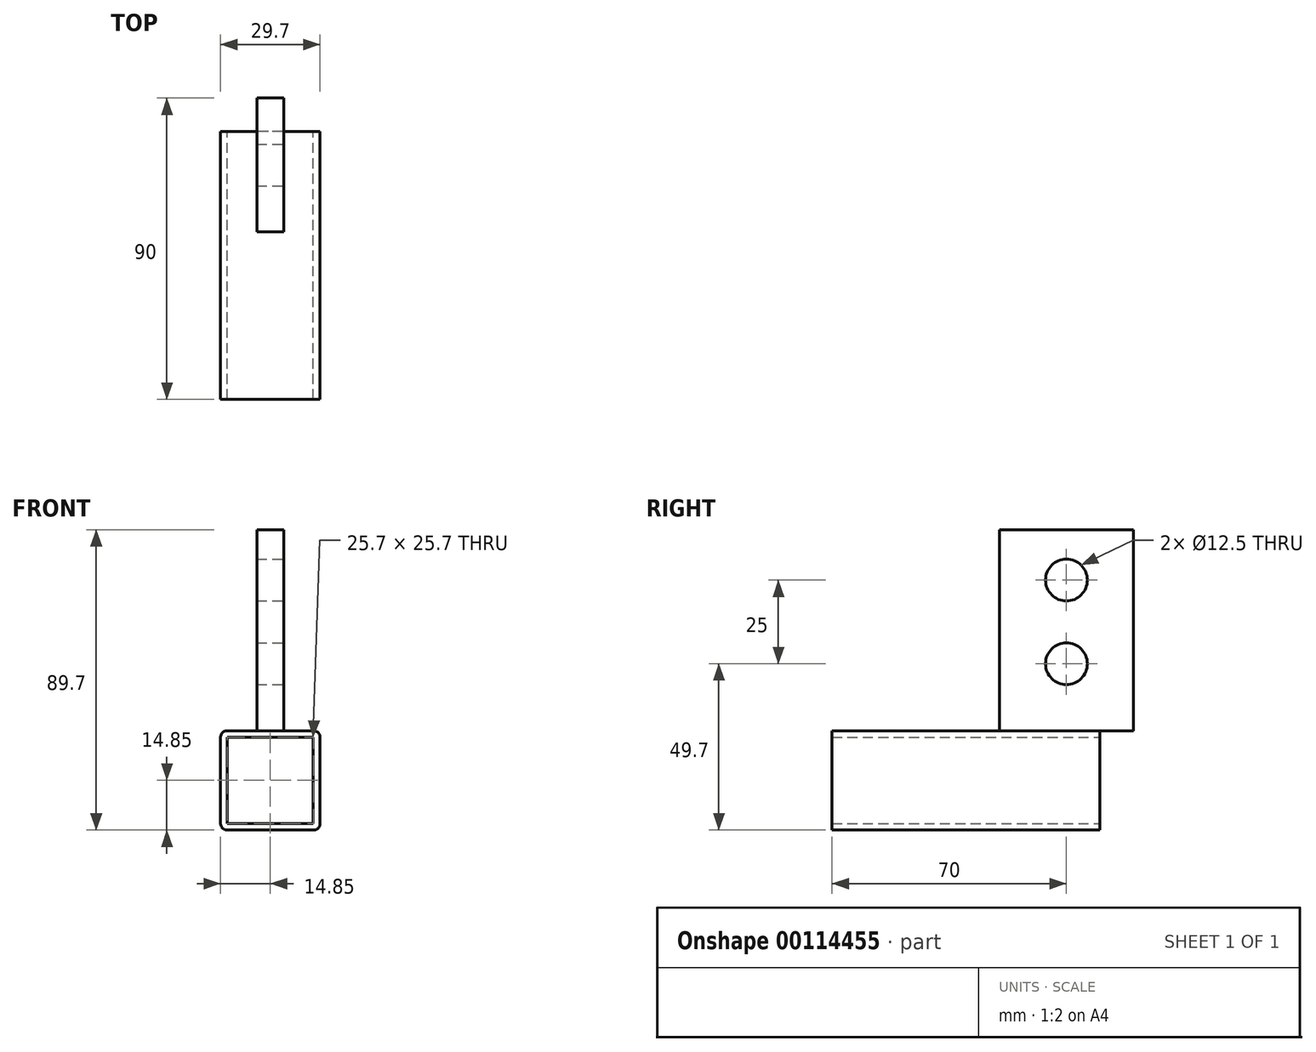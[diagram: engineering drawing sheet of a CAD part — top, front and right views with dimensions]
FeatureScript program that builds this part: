
annotation { "Feature Type Name" : "Feature", "Feature Type Description" : "" }
export const myFeature = defineFeature(function(context is Context, id is Id, definition is map)
    precondition{}
    {
        {
            var Q0;
            Q0=qCreatedBy(makeId("Front.planeOp"),FACE);
            var sketch = newSketch(context, id + "F0", { "sketchPlane" : qUnion([Q0])});
            skLineSegment(sketch, "E0.bottom", {"start": v(12.85, -14.85) * mm, "end": v(-12.85, -14.85) * mm});
            skLineSegment(sketch, "E0.top", {"start": v(12.85, 14.85) * mm, "end": v(-12.85, 14.85) * mm});
            skLineSegment(sketch, "E0.left", {"start": v(14.85, -12.85) * mm, "end": v(14.85, 12.85) * mm});
            skLineSegment(sketch, "E0.right", {"start": v(-14.85, -12.85) * mm, "end": v(-14.85, 12.85) * mm});
            skPoint(sketch, "E0.middle", {"position": v(0, 0) * mm});
            skLineSegment(sketch, "E1.0", {"start": v(-12.85, -12.85) * mm, "end": v(-12.85, 12.85) * mm});
            skLineSegment(sketch, "E1.1", {"start": v(12.85, -12.85) * mm, "end": v(-12.85, -12.85) * mm});
            skLineSegment(sketch, "E1.2", {"start": v(12.85, -12.85) * mm, "end": v(12.85, 12.85) * mm});
            skLineSegment(sketch, "E1.3", {"start": v(12.85, 12.85) * mm, "end": v(-12.85, 12.85) * mm});
            skPoint(sketch, "E2.visualSharp", {"position": v(14.85, 14.85) * mm});
            skArc(sketch, "E2.filletArc", {"start": v(14.85, 12.85) * mm, "mid": v(14.26, 14.26) * mm, "end": v(12.85, 14.85) * mm});
            skPoint(sketch, "E3.visualSharp", {"position": v(14.85, -14.85) * mm});
            skArc(sketch, "E3.filletArc", {"start": v(12.85, -14.85) * mm, "mid": v(14.26, -14.26) * mm, "end": v(14.85, -12.85) * mm});
            skPoint(sketch, "E4.visualSharp", {"position": v(-14.85, -14.85) * mm});
            skArc(sketch, "E4.filletArc", {"start": v(-14.85, -12.85) * mm, "mid": v(-14.26, -14.26) * mm, "end": v(-12.85, -14.85) * mm});
            skPoint(sketch, "E5.visualSharp", {"position": v(-14.85, 14.85) * mm});
            skArc(sketch, "E5.filletArc", {"start": v(-12.85, 14.85) * mm, "mid": v(-14.26, 14.26) * mm, "end": v(-14.85, 12.85) * mm});
            skSolve(sketch);
        }
        {
            var Q0;
            Q0=makeQuery(id+"F0.imprint","IMPRINT",FACE,{"disambiguationData":[TD([[makeQuery(id+"F0.imprint","IMPRINT",EDGE,{"derivedFrom":sQuery(id+"F0.wireOp",EDGE,"E0.bottom")}),-1.0]])]});
            extrude(context, id + "F1", {"entities" : qUnion([Q0]), "depth" : 80 * mm});
        }
        {
            var Q0;
            Q0=makeQuery(id+"F1.opExtrude","SWEPT_FACE",FACE,{"disambiguationData":[OSD([sQuery(id+"F0.wireOp",EDGE,"E0.top")])]});
            var sketch = newSketch(context, id + "F2", { "sketchPlane" : qUnion([Q0])});
            skLineSegment(sketch, "E6.bottom", {"start": v(4, -30) * mm, "end": v(-4, -30) * mm});
            skLineSegment(sketch, "E6.top", {"start": v(4, 10) * mm, "end": v(-4, 10) * mm});
            skLineSegment(sketch, "E6.left", {"start": v(4, -30) * mm, "end": v(4, 10) * mm});
            skLineSegment(sketch, "E6.right", {"start": v(-4, -30) * mm, "end": v(-4, 10) * mm});
            skPoint(sketch, "E6.middle", {"position": v(0, -10) * mm});
            skSolve(sketch);
        }
        {
            var Q0;
            Q0=makeQuery(id+"F2.imprint","IMPRINT",FACE,{"disambiguationData":[TD([[makeQuery(id+"F2.imprint","IMPRINT",EDGE,{"derivedFrom":sQuery(id+"F2.wireOp",EDGE,"E6.bottom")}),-1.0]])]});
            var Q1;
            {var subQ0=sQuery(id+"F2.wireOp",EDGE,"E6.top");Q1=makeQuery(id+"F2.imprint","IMPRINT",FACE,{"disambiguationData":[TD([[makeQuery(id+"F2.imprint","IMPRINT",EDGE,{"derivedFrom":subQ0}),1.0]])]});}
            extrude(context, id + "F3", {"entities" : qUnion([Q0, Q1]), "operationType" : NewBodyOperationType.ADD, "depth" : 60 * mm});
        }
        {
            var Q0;
            Q0=makeQuery(id+"F3.opExtrude","SWEPT_FACE",FACE,{"disambiguationData":[OSD([sQuery(id+"F2.wireOp",EDGE,"E6.left")])]});
            var sketch = newSketch(context, id + "F4", { "sketchPlane" : qUnion([Q0])});
            skCircle(sketch, "E7", {"center": v(-10, 59.85) * mm, "radius": 6.25 * mm});
            skCircle(sketch, "E8", {"center": v(-10, 34.85) * mm, "radius": 6.25 * mm});
            skSolve(sketch);
        }
        {
            var Q0;
            Q0=makeQuery(id+"F4.imprint","IMPRINT",FACE,{"disambiguationData":[TD([[makeQuery(id+"F4.imprint","IMPRINT",EDGE,{"derivedFrom":sQuery(id+"F4.wireOp",EDGE,"E8")}),1.0]])]});
            var Q1;
            Q1=makeQuery(id+"F4.imprint","IMPRINT",FACE,{"disambiguationData":[TD([[makeQuery(id+"F4.imprint","IMPRINT",EDGE,{"derivedFrom":sQuery(id+"F4.wireOp",EDGE,"E7")}),1.0]])]});
            extrude(context, id + "F5", {"entities" : qUnion([Q0, Q1]), "operationType" : NewBodyOperationType.REMOVE, "oppositeDirection" : true, "depth" : 25 * mm});
        }
    });
